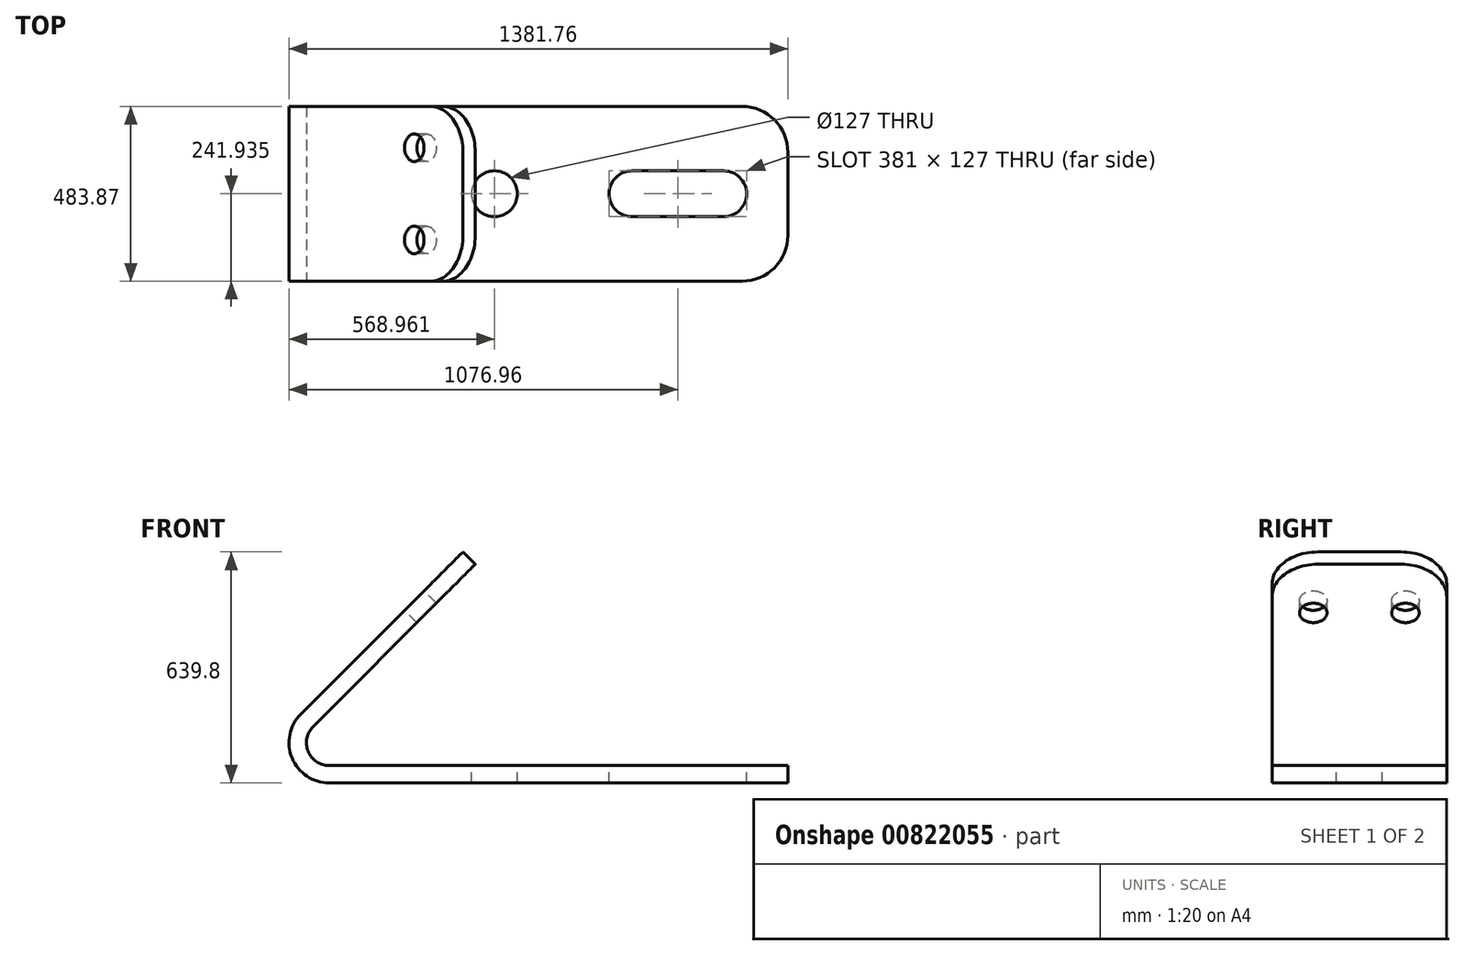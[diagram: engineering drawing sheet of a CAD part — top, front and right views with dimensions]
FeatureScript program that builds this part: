
annotation { "Feature Type Name" : "Feature", "Feature Type Description" : "" }
export const myFeature = defineFeature(function(context is Context, id is Id, definition is map)
    precondition{}
    {
        {
            var Q0;
            Q0=qCreatedBy(makeId("Front.planeOp"),FACE);
            var sketch = newSketch(context, id + "F0", { "sketchPlane" : qUnion([Q0])});
            skLineSegment(sketch, "E0", {"start": v(596.98, 24.17) * mm, "end": v(-673.02, 24.17) * mm});
            skLineSegment(sketch, "E1", {"start": v(596.98, 24.17) * mm, "end": v(596.98, -24.09) * mm});
            skLineSegment(sketch, "E2", {"start": v(596.98, -24.09) * mm, "end": v(-673.02, -24.09) * mm});
            skLineSegment(sketch, "E3", {"start": v(-717.92, 132.57) * mm, "end": v(-268.9, 581.59) * mm});
            skLineSegment(sketch, "E4", {"start": v(-268.9, 581.59) * mm, "end": v(-303.03, 615.71) * mm});
            skLineSegment(sketch, "E5", {"start": v(-303.03, 615.71) * mm, "end": v(-752.05, 166.7) * mm});
            skArc(sketch, "E6", {"start": v(-752.05, 166.7) * mm, "mid": v(-776.27, 44.9) * mm, "end": v(-673.02, -24.09) * mm});
            skArc(sketch, "E7", {"start": v(-717.92, 132.57) * mm, "mid": v(-731.69, 63.37) * mm, "end": v(-673.02, 24.17) * mm});
            skSolve(sketch);
        }
        {
            var Q0;
            Q0 = qSketchRegion(id + "F0", true);
            extrude(context, id + "F1", {"entities" : qUnion([Q0]), "oppositeDirection" : true, "depth" : 483.87 * mm, "offsetDistance" : 25.4 * mm});
        }
        {
            var Q0;
            Q0=makeQuery(id+"F1.opExtrude","CAP_EDGE",EDGE,{"disambiguationData":[OSD([sQuery(id+"F0.wireOp",EDGE,"E1")])],"isStart":true});
            var Q1;
            Q1=makeQuery(id+"F1.opExtrude","CAP_EDGE",EDGE,{"disambiguationData":[OSD([sQuery(id+"F0.wireOp",EDGE,"E1")])],"isStart":false});
            var Q2;
            Q2=makeQuery(id+"F1.opExtrude","CAP_EDGE",EDGE,{"disambiguationData":[OSD([sQuery(id+"F0.wireOp",EDGE,"E4")])],"isStart":true});
            var Q3;
            Q3=makeQuery(id+"F1.opExtrude","CAP_EDGE",EDGE,{"disambiguationData":[OSD([sQuery(id+"F0.wireOp",EDGE,"E4")])],"isStart":false});
            fillet(context, id + "F2", {"entities" : qUnion([Q0, Q1, Q2, Q3]), "radius" : 127 * mm, "tangentPropagation" : true, "allowEdgeOverflow" : false});
        }
        {
            var Q0;
            Q0=makeQuery(id+"F1.opExtrude","SWEPT_FACE",FACE,{"disambiguationData":[OSD([sQuery(id+"F0.wireOp",EDGE,"E5")])]});
            var sketch = newSketch(context, id + "F3", { "sketchPlane" : qUnion([Q0])});
            skCircle(sketch, "E8", {"center": v(-369.57, 30.6) * mm, "radius": 38.1 * mm});
            skCircle(sketch, "E9", {"center": v(-114.3, 30.6) * mm, "radius": 38.1 * mm});
            skSolve(sketch);
        }
        {
            var Q0;
            Q0 = qSketchRegion(id + "F3", true);
            var Q1;
            Q1=makeQuery(id+"F1.opExtrude","SWEPT_FACE",FACE,{"disambiguationData":[OSD([sQuery(id+"F0.wireOp",EDGE,"E3")])]});
            extrude(context, id + "F4", {"entities" : qUnion([Q0]), "operationType" : NewBodyOperationType.REMOVE, "endBound" : BoundingType.UP_TO_SURFACE, "oppositeDirection" : true, "depth" : 25.4 * mm, "endBoundEntityFace" : qUnion([Q1]), "offsetDistance" : 25.4 * mm});
        }
        {
            var Q0;
            Q0=makeQuery(id+"F1.opExtrude","SWEPT_FACE",FACE,{"disambiguationData":[OSD([sQuery(id+"F0.wireOp",EDGE,"E0")])]});
            var sketch = newSketch(context, id + "F5", { "sketchPlane" : qUnion([Q0])});
            skCircle(sketch, "E10", {"center": v(-215.82, 241.94) * mm, "radius": 63.5 * mm});
            skPoint(sketch, "E10.centerSnap0", {"position": v(596.98, 241.94) * mm});
            skLineSegment(sketch, "E11", {"start": v(482.68, 241.94) * mm, "end": v(101.68, 241.94) * mm});
            skLineSegment(sketch, "E12", {"start": v(101.68, 241.94) * mm, "end": v(101.68, 241.94) * mm});
            skLineSegment(sketch, "E13", {"start": v(165.18, 305.44) * mm, "end": v(419.18, 305.44) * mm});
            skLineSegment(sketch, "E14", {"start": v(482.68, 241.94) * mm, "end": v(482.68, 241.94) * mm});
            skPoint(sketch, "E15.visualSharp", {"position": v(101.68, 305.44) * mm});
            skArc(sketch, "E15.filletArc", {"start": v(165.18, 305.44) * mm, "mid": v(120.28, 286.84) * mm, "end": v(101.68, 241.94) * mm});
            skPoint(sketch, "E16.visualSharp", {"position": v(482.68, 305.44) * mm});
            skArc(sketch, "E16.filletArc", {"start": v(482.68, 241.94) * mm, "mid": v(464.08, 286.84) * mm, "end": v(419.18, 305.44) * mm});
            skArc(sketch, "E17.MirrorCS", {"start": v(165.18, 178.44) * mm, "mid": v(120.28, 197.03) * mm, "end": v(101.68, 241.94) * mm});
            skLineSegment(sketch, "E18.MirrorCS", {"start": v(165.18, 178.44) * mm, "end": v(419.18, 178.44) * mm});
            skArc(sketch, "E19.MirrorCS", {"start": v(482.68, 241.94) * mm, "mid": v(464.08, 197.03) * mm, "end": v(419.18, 178.44) * mm});
            skSolve(sketch);
        }
        {
            var Q0;
            Q0 = qSketchRegion(id + "F5", true);
            var Q1;
            Q1=makeQuery(id+"F1.opExtrude","SWEPT_FACE",FACE,{"disambiguationData":[OSD([sQuery(id+"F0.wireOp",EDGE,"E2")])]});
            extrude(context, id + "F6", {"entities" : qUnion([Q0]), "operationType" : NewBodyOperationType.REMOVE, "endBound" : BoundingType.UP_TO_SURFACE, "oppositeDirection" : true, "depth" : 25.4 * mm, "endBoundEntityFace" : qUnion([Q1]), "offsetDistance" : 25.4 * mm});
        }
    });
